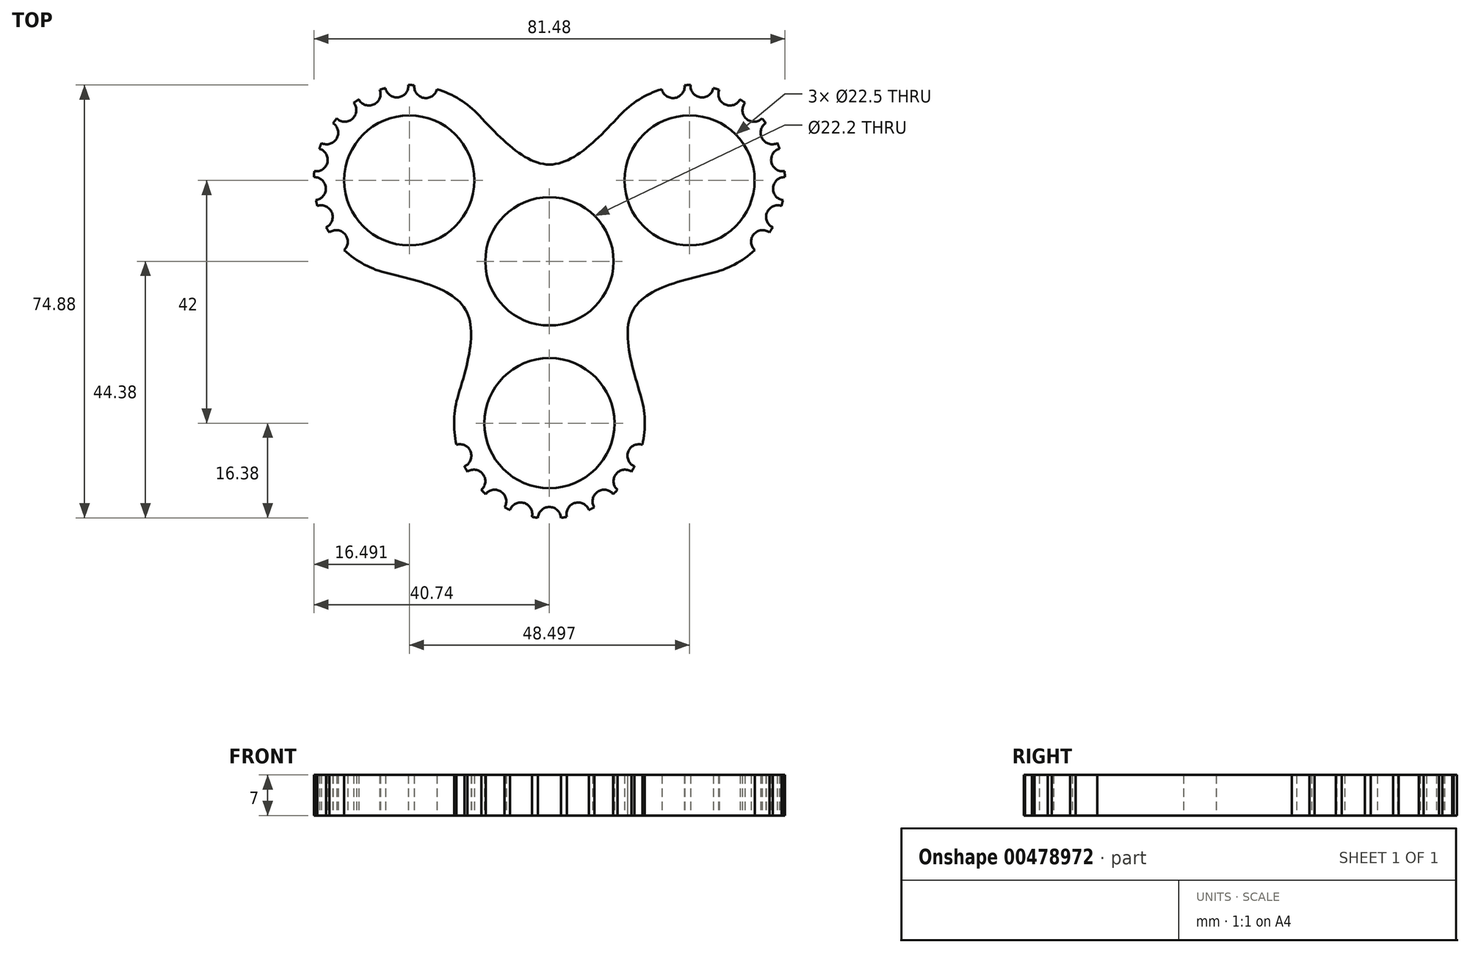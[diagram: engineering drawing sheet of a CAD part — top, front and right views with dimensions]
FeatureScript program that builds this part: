
annotation { "Feature Type Name" : "Feature", "Feature Type Description" : "" }
export const myFeature = defineFeature(function(context is Context, id is Id, definition is map)
    precondition{}
    {
        {
            var Q0;
            Q0=qCreatedBy(makeId("Top.planeOp"),FACE);
            var sketch = newSketch(context, id + "F0", { "sketchPlane" : qUnion([Q0])});
            skCircle(sketch, "E0", {"center": v(0, 0) * mm, "radius": 11.1 * mm});
            skCircle(sketch, "E1", {"center": v(-24.25, 14) * mm, "radius": 11.25 * mm});
            skCircle(sketch, "E2", {"center": v(24.25, 14) * mm, "radius": 11.25 * mm});
            skCircle(sketch, "E3", {"center": v(0, -28) * mm, "radius": 11.25 * mm});
            skLineSegment(sketch, "E4", {"start": v(-24.25, 14) * mm, "end": v(0, -28) * mm, "construction": true});
            skLineSegment(sketch, "E5", {"start": v(24.25, 14) * mm, "end": v(0, -28) * mm, "construction": true});
            skLineSegment(sketch, "E6", {"start": v(24.25, 14) * mm, "end": v(-24.25, 14) * mm, "construction": true});
            skLineSegment(sketch, "E7", {"start": v(0, 14) * mm, "end": v(0, 0) * mm, "construction": true});
            skLineSegment(sketch, "E8", {"start": v(0, 0) * mm, "end": v(12.12, -7) * mm, "construction": true});
            skLineSegment(sketch, "E9", {"start": v(0, 0) * mm, "end": v(-12.12, -7) * mm, "construction": true});
            skCircle(sketch, "E10", {"center": v(24.25, 14) * mm, "radius": 16.5 * mm});
            skCircle(sketch, "E11", {"center": v(-24.25, 14) * mm, "radius": 16.5 * mm});
            skCircle(sketch, "E12", {"center": v(0, -28) * mm, "radius": 16.5 * mm});
            skCircle(sketch, "E13", {"center": v(0, 0) * mm, "radius": 16.75 * mm, "construction": true});
            skLineSegment(sketch, "E14", {"start": v(-27.96, -2.08) * mm, "end": v(-15.78, -23.17) * mm, "construction": true});
            skLineSegment(sketch, "E15", {"start": v(15.78, -23.17) * mm, "end": v(27.96, -2.08) * mm, "construction": true});
            skLineSegment(sketch, "E16", {"start": v(12.18, 25.25) * mm, "end": v(-12.18, 25.25) * mm, "construction": true});
            skLineSegment(sketch, "E17", {"start": v(0, 0) * mm, "end": v(38.54, 22.25) * mm, "construction": true});
            skLineSegment(sketch, "E18", {"start": v(24.25, 14) * mm, "end": v(21.38, 30.25) * mm, "construction": true});
            skCircle(sketch, "E19", {"center": v(21.38, 30.25) * mm, "radius": 2 * mm});
            skCircle(sketch, "E20.1.0", {"center": v(26.4, 30.36) * mm, "radius": 2 * mm});
            skCircle(sketch, "E20.2.0", {"center": v(31.22, 28.95) * mm, "radius": 2 * mm});
            skCircle(sketch, "E20.3.0", {"center": v(35.4, 26.17) * mm, "radius": 2 * mm});
            skCircle(sketch, "E20.4.0", {"center": v(38.54, 22.25) * mm, "radius": 2 * mm});
            skCircle(sketch, "E20.5.0", {"center": v(40.36, 17.57) * mm, "radius": 2 * mm});
            skLineSegment(sketch, "E20.anchor2", {"start": v(24.25, 14) * mm, "end": v(36.89, 3.4) * mm, "construction": true});
            skCircle(sketch, "E21.1.0", {"center": v(-36.89, 3.4) * mm, "radius": 2 * mm});
            skCircle(sketch, "E21.1.1", {"center": v(-39.5, 7.69) * mm, "radius": 2 * mm});
            skCircle(sketch, "E21.1.2", {"center": v(-40.69, 12.56) * mm, "radius": 2 * mm});
            skCircle(sketch, "E21.1.3", {"center": v(-40.36, 17.57) * mm, "radius": 2 * mm});
            skCircle(sketch, "E21.1.4", {"center": v(-38.54, 22.25) * mm, "radius": 2 * mm});
            skCircle(sketch, "E21.1.5", {"center": v(-21.38, 30.25) * mm, "radius": 2 * mm});
            skCircle(sketch, "E21.2.0", {"center": v(15.5, -33.64) * mm, "radius": 2 * mm});
            skCircle(sketch, "E21.2.1", {"center": v(13.1, -38.04) * mm, "radius": 2 * mm});
            skCircle(sketch, "E21.2.2", {"center": v(9.46, -41.52) * mm, "radius": 2 * mm});
            skCircle(sketch, "E21.2.3", {"center": v(4.96, -43.74) * mm, "radius": 2 * mm});
            skCircle(sketch, "E21.2.4", {"center": v(0, -44.5) * mm, "radius": 2 * mm});
            skCircle(sketch, "E21.2.5", {"center": v(-15.5, -33.64) * mm, "radius": 2 * mm});
            skCircle(sketch, "E22", {"center": v(24.25, 14) * mm, "radius": 10 * mm});
            skCircle(sketch, "E23", {"center": v(0, -28) * mm, "radius": 10 * mm});
            skCircle(sketch, "E24", {"center": v(-24.25, 14) * mm, "radius": 10 * mm});
            skLineSegment(sketch, "E25", {"start": v(12.12, -7) * mm, "end": v(14.5, -8.38) * mm});
            skFitSpline(sketch, "E26", {"points": [v(27.96, -2.08) * mm, v(14.5, -8.38) * mm, v(15.78, -23.17) * mm], "startDerivative": vector(-34.36, -7.92) * mm, "endDerivative": vector(10.32, -33.72) * mm});
            skLineSegment(sketch, "E27", {"start": v(0, 14) * mm, "end": v(0, 16.75) * mm});
            skLineSegment(sketch, "E28", {"start": v(-12.12, -7) * mm, "end": v(-14.5, -8.38) * mm});
            skFitSpline(sketch, "E29", {"points": [v(-27.96, -2.08) * mm, v(-14.5, -8.37) * mm, v(-15.78, -23.17) * mm], "startDerivative": vector(34.36, -7.92) * mm, "endDerivative": vector(-10.32, -33.72) * mm});
            skFitSpline(sketch, "E30", {"points": [v(-12.18, 25.25) * mm, v(0, 16.75) * mm, v(12.18, 25.25) * mm], "startDerivative": vector(24.04, -25.8) * mm, "endDerivative": vector(24.04, 25.8) * mm});
            skCircle(sketch, "E31.1.6.0", {"center": v(40.69, 12.56) * mm, "radius": 2 * mm});
            skCircle(sketch, "E31.1.7.0", {"center": v(39.5, 7.69) * mm, "radius": 2 * mm});
            skCircle(sketch, "E31.1.8.0", {"center": v(36.89, 3.4) * mm, "radius": 2 * mm});
            skCircle(sketch, "E32.1.2", {"center": v(-26.4, 30.36) * mm, "radius": 2 * mm});
            skCircle(sketch, "E32.1.3", {"center": v(-31.22, 28.95) * mm, "radius": 2 * mm});
            skCircle(sketch, "E32.1.4", {"center": v(-35.4, 26.17) * mm, "radius": 2 * mm});
            skCircle(sketch, "E32.2.2", {"center": v(-13.1, -38.04) * mm, "radius": 2 * mm});
            skCircle(sketch, "E32.2.3", {"center": v(-9.46, -41.52) * mm, "radius": 2 * mm});
            skCircle(sketch, "E32.2.4", {"center": v(-4.96, -43.74) * mm, "radius": 2 * mm});
            skSolve(sketch);
        }
        {
            var Q0;
            Q0=makeQuery(id+"F0.imprint","IMPRINT",FACE,{"disambiguationData":[TD([[makeQuery(id+"F0.imprint","IMPRINT",EDGE,{"derivedFrom":sQuery(id+"F0.wireOp",EDGE,"E1")}),-1.0]])]});
            var Q1;
            Q1=makeQuery(id+"F0.imprint","IMPRINT",FACE,{"disambiguationData":[TD([[makeQuery(id+"F0.imprint","IMPRINT",EDGE,{"derivedFrom":sQuery(id+"F0.wireOp",EDGE,"E0")}),-1.0]])]});
            var Q2;
            Q2=makeQuery(id+"F0.imprint","IMPRINT",FACE,{"disambiguationData":[TD([[makeQuery(id+"F0.imprint","IMPRINT",EDGE,{"derivedFrom":sQuery(id+"F0.wireOp",EDGE,"E2")}),-1.0]])]});
            var Q3;
            Q3=makeQuery(id+"F0.imprint","IMPRINT",FACE,{"disambiguationData":[TD([[makeQuery(id+"F0.imprint","IMPRINT",EDGE,{"derivedFrom":sQuery(id+"F0.wireOp",EDGE,"E3")}),-1.0]])]});
            extrude(context, id + "F1", {"entities" : qUnion([Q0, Q1, Q2, Q3]), "depth" : 7 * mm});
        }
    });
